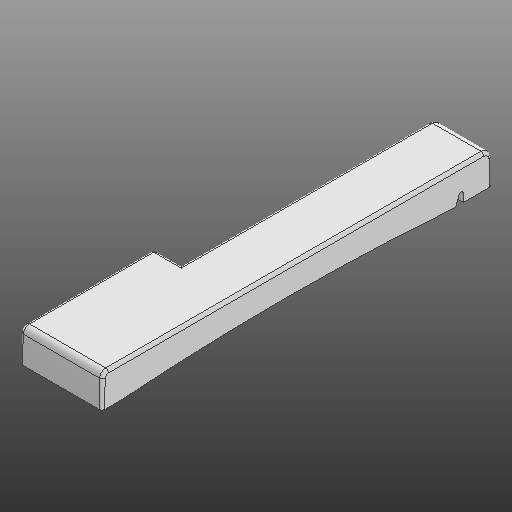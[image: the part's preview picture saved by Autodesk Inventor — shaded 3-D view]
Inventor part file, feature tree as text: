
AUTODESK INVENTOR PART (.ipt)
format: ipt  version: 2020 (Build 240168000, 168)  size: 315,904 bytes
history: native  units: in
note: dims shown in document units (in); Inventor stores cm internally (conversion verified against a paired STEP export)
features: extrude x4, other x3, fillet x2
ambient origin geometry x8: Origin, YZ Plane, XZ Plane, XY Plane, X Axis, Y Axis, Z Axis, Center Point
bodies: Solid1 (feature_tree)
feature tree (9):
  other  "Slot Start Plane"
  other  "Key Profile"
  extrude  "Upper (u)"  TaperAngle=0.0deg  [1 undecoded]
  extrude  "Lower (d)"  TaperAngle=0.0deg  [1 undecoded]
  extrude  "Protrusion Cutout"  Depth=0.0591in
  fillet  "Front Fillet"  Radius=0.1374in
  extrude  "Slot"  [1 undecoded]
  fillet  "Edge Softening"  Radius=0.0787in
  other  "Slot Sketch"
note: 3 required parameter values undecoded (feature->parameter linkage not recoverable at this tier; creation-order binding heuristic only, values carry confidence <= 0.55)
